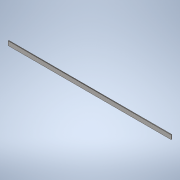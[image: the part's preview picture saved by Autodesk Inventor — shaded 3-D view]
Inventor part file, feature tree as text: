
AUTODESK INVENTOR PART (.ipt)
format: ipt  version: 2021 (Build 250183000, 183)  size: 99,328 bytes
history: native  units: mm
features: extrude x1, sketch x1
ambient origin geometry x8: Origin, YZ Plane, XZ Plane, XY Plane, X Axis, Y Axis, Z Axis, Center Point
bodies: Solid1 (feature_tree)
feature tree (2):
  extrude  "Extrusion1"  Depth=1994.0mm
  sketch  "Sketch1"  dims[d0=50.0mm d1=1994.0mm d2=10.0mm d3=0.0mm]
